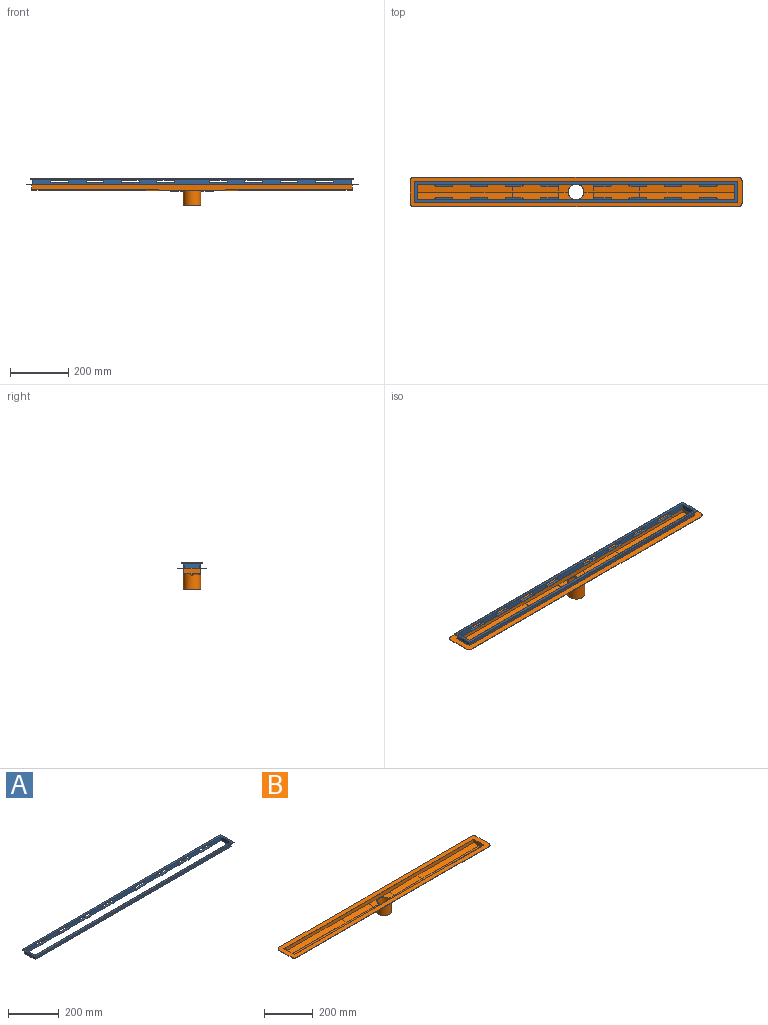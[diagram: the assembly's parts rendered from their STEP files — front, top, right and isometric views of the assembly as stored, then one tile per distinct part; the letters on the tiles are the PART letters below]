
ASSEMBLY  parts=2 mates=1
PART A: 212 faces, bbox 1112.8x73x20.6 mm
  f0: plane 1093.79x20.64mm, normal (0,1,0), area 17992.5mm2, adj f6,f7,f9,f12,f13,f17,f19,f23
  f1: plane 1096.96x19.05mm, normal (0,-1,0), area 17088.3mm2, adj f2,f6,f10,f18,f25,f32,f39,f40
  f2: plane 1109.66x69.85mm, normal (0,0,-1), area 14818.5mm2, adj f1,f5,f10,f11,f61,f63,f114,f115
  f3: plane 1112.84x3.18mm, normal (0,-1,0), area 3533.3mm2, adj f4,f7,f8,f112
  f4: plane 1112.84x73.03mm, normal (0,0,-1), area 3755mm2, adj f3,f5,f8,f11,f62,f63,f112,f115
  f5: plane 1109.66x1.59mm, normal (0,1,0), area 1761.6mm2, adj f2,f4,f11,f115
  f6: plane 1096.96x57.15mm, normal (0,0,-1), area 3654.2mm2, adj f0,f1,f9,f10,f60,f61,f113,f114
  f7: plane 1112.84x73.03mm, normal (0,0,1), area 22227.8mm2, adj f0,f3,f8,f9,f60,f62,f112,f113
  f8: plane 73.03x3.18mm, normal (1,0,0), area 231.9mm2, adj f3,f4,f7,f62
  f9: plane 53.98x20.64mm, normal (-1,0,0), area 1113.9mm2, adj f0,f6,f7,f60
  f10: plane 57.15x19.05mm, normal (1,0,0), area 1088.7mm2, adj f1,f2,f6,f61
  f11: plane 69.85x1.59mm, normal (-1,0,0), area 110.9mm2, adj f2,f4,f5,f63
  f12: plane 4.13x1.59mm, normal (-1,0,0), area 6.6mm2, adj f0,f16,f17,f18
  f13: plane 4.13x1.59mm, normal (1,0,0), area 6.6mm2, adj f0,f14,f17,f18
  f14: cylinder r=3.81mm len=3.81mm, axis (0,0,1), area 9.5mm2, adj f13,f15,f17,f18
  f15: plane 53.15x1.59mm, normal (0,1,0), area 84.4mm2, adj f14,f16,f17,f18
  f16: cylinder r=3.81mm len=3.81mm, axis (0,0,1), area 9.5mm2, adj f12,f15,f17,f18
  f17: plane 60.77x7.94mm, normal (0,0,-1), area 476.1mm2, adj f0,f12,f13,f14,f15,f16
  f18: plane 60.77x9.53mm, normal (0,0,1), area 572.6mm2, adj f1,f12,f13,f14,f15,f16,f40,f44
  f19: plane 4.13x1.59mm, normal (1,0,0), area 6.6mm2, adj f0,f20,f24,f25
  f20: cylinder r=3.81mm len=3.81mm, axis (0,0,1), area 9.5mm2, adj f19,f21,f24,f25
  f21: plane 53.15x1.59mm, normal (0,1,0), area 84.4mm2, adj f20,f22,f24,f25
  f22: cylinder r=3.81mm len=3.81mm, axis (0,0,1), area 9.5mm2, adj f21,f23,f24,f25
  f23: plane 4.13x1.59mm, normal (-1,0,0), area 6.6mm2, adj f0,f22,f24,f25
  f24: plane 60.77x7.94mm, normal (0,0,-1), area 476.1mm2, adj f0,f19,f20,f21,f22,f23
  f25: plane 60.77x9.53mm, normal (0,0,1), area 572.6mm2, adj f1,f19,f20,f21,f22,f23,f45,f49
  f26: plane 4.13x1.59mm, normal (1,0,0), area 6.6mm2, adj f0,f27,f31,f32
  f27: cylinder r=3.81mm len=3.81mm, axis (0,0,1), area 9.5mm2, adj f26,f28,f31,f32
  f28: plane 53.15x1.59mm, normal (0,1,0), area 84.4mm2, adj f27,f29,f31,f32
  f29: cylinder r=3.81mm len=3.81mm, axis (0,0,1), area 9.5mm2, adj f28,f30,f31,f32
  f30: plane 4.13x1.59mm, normal (-1,0,0), area 6.6mm2, adj f0,f29,f31,f32
  f31: plane 60.77x7.94mm, normal (0,0,-1), area 476.1mm2, adj f0,f26,f27,f28,f29,f30
  f32: plane 60.77x9.53mm, normal (0,0,1), area 572.6mm2, adj f1,f26,f27,f28,f29,f30,f50,f54
  f33: plane 4.13x1.59mm, normal (1,0,0), area 6.6mm2, adj f0,f34,f38,f39
  f34: cylinder r=3.81mm len=3.81mm, axis (0,0,1), area 9.5mm2, adj f33,f35,f38,f39
  f35: plane 53.15x1.59mm, normal (0,1,0), area 84.4mm2, adj f34,f36,f38,f39
  f36: cylinder r=3.81mm len=3.81mm, axis (0,0,1), area 9.5mm2, adj f35,f37,f38,f39
  f37: plane 4.13x1.59mm, normal (-1,0,0), area 6.6mm2, adj f0,f36,f38,f39
  f38: plane 60.77x7.94mm, normal (0,0,-1), area 476.1mm2, adj f0,f33,f34,f35,f36,f37
  f39: plane 60.77x9.53mm, normal (0,0,1), area 572.6mm2, adj f1,f33,f34,f35,f36,f37,f56,f57
  f40: plane 4.13x1.59mm, normal (1,0,0), area 6.6mm2, adj f0,f1,f18,f41
  f41: cylinder r=3.81mm len=3.81mm, axis (0,1,0), area 9.5mm2, adj f0,f1,f40,f42
  f42: plane 53.15x1.59mm, normal (0,0,-1), area 84.4mm2, adj f0,f1,f41,f43
  f43: cylinder r=3.81mm len=3.81mm, axis (0,1,0), area 9.5mm2, adj f0,f1,f42,f44
  f44: plane 4.13x1.59mm, normal (-1,0,0), area 6.6mm2, adj f0,f1,f18,f43
  f45: plane 4.13x1.59mm, normal (1,0,0), area 6.6mm2, adj f0,f1,f25,f46
  f46: cylinder r=3.81mm len=3.81mm, axis (0,1,0), area 9.5mm2, adj f0,f1,f45,f47
  f47: plane 53.15x1.59mm, normal (0,0,-1), area 84.4mm2, adj f0,f1,f46,f48
  f48: cylinder r=3.81mm len=3.81mm, axis (0,1,0), area 9.5mm2, adj f0,f1,f47,f49
  f49: plane 4.13x1.59mm, normal (-1,0,0), area 6.6mm2, adj f0,f1,f25,f48
  f50: plane 4.13x1.59mm, normal (1,0,0), area 6.6mm2, adj f0,f1,f32,f51
  f51: cylinder r=3.81mm len=3.81mm, axis (0,1,0), area 9.5mm2, adj f0,f1,f50,f52
  f52: plane 53.15x1.59mm, normal (0,0,-1), area 84.4mm2, adj f0,f1,f51,f53
  f53: cylinder r=3.81mm len=3.81mm, axis (0,1,0), area 9.5mm2, adj f0,f1,f52,f54
  f54: plane 4.13x1.59mm, normal (-1,0,0), area 6.6mm2, adj f0,f1,f32,f53
  f55: cylinder r=3.81mm len=3.81mm, axis (0,1,0), area 9.5mm2, adj f0,f1,f56,f59
  f56: plane 4.13x1.59mm, normal (-1,0,0), area 6.6mm2, adj f0,f1,f39,f55
  f57: plane 4.13x1.59mm, normal (1,0,0), area 6.6mm2, adj f0,f1,f39,f58
  f58: cylinder r=3.81mm len=3.81mm, axis (0,1,0), area 9.5mm2, adj f0,f1,f57,f59
  f59: plane 53.15x1.59mm, normal (0,0,-1), area 84.4mm2, adj f0,f1,f55,f58
  f60: plane 1093.79x20.64mm, normal (0,-1,0), area 17992.5mm2, adj f6,f7,f9,f64,f65,f69,f71,f75
  f61: plane 1096.96x19.05mm, normal (0,1,0), area 17088.3mm2, adj f2,f6,f10,f70,f77,f84,f91,f92
  f62: plane 1112.84x3.18mm, normal (0,1,0), area 3533.3mm2, adj f4,f7,f8,f112
  f63: plane 1109.66x1.59mm, normal (0,-1,0), area 1761.6mm2, adj f2,f4,f11,f115
  f64: plane 4.13x1.59mm, normal (-1,0,0), area 6.6mm2, adj f60,f68,f69,f70
  f65: plane 4.13x1.59mm, normal (1,0,0), area 6.6mm2, adj f60,f66,f69,f70
  f66: cylinder r=3.81mm len=3.81mm, axis (0,0,1), area 9.5mm2, adj f65,f67,f69,f70
  f67: plane 53.15x1.59mm, normal (0,-1,0), area 84.4mm2, adj f66,f68,f69,f70
  f68: cylinder r=3.81mm len=3.81mm, axis (0,0,1), area 9.5mm2, adj f64,f67,f69,f70
  f69: plane 60.77x7.94mm, normal (0,0,-1), area 476.1mm2, adj f60,f64,f65,f66,f67,f68
  f70: plane 60.77x9.53mm, normal (0,0,1), area 572.6mm2, adj f61,f64,f65,f66,f67,f68,f92,f96
  f71: plane 4.13x1.59mm, normal (1,0,0), area 6.6mm2, adj f60,f72,f76,f77
  f72: cylinder r=3.81mm len=3.81mm, axis (0,0,1), area 9.5mm2, adj f71,f73,f76,f77
  f73: plane 53.15x1.59mm, normal (0,-1,0), area 84.4mm2, adj f72,f74,f76,f77
  f74: cylinder r=3.81mm len=3.81mm, axis (0,0,1), area 9.5mm2, adj f73,f75,f76,f77
  f75: plane 4.13x1.59mm, normal (-1,0,0), area 6.6mm2, adj f60,f74,f76,f77
  f76: plane 60.77x7.94mm, normal (0,0,-1), area 476.1mm2, adj f60,f71,f72,f73,f74,f75
  f77: plane 60.77x9.53mm, normal (0,0,1), area 572.6mm2, adj f61,f71,f72,f73,f74,f75,f97,f101
  f78: plane 4.13x1.59mm, normal (1,0,0), area 6.6mm2, adj f60,f79,f83,f84
  f79: cylinder r=3.81mm len=3.81mm, axis (0,0,1), area 9.5mm2, adj f78,f80,f83,f84
  f80: plane 53.15x1.59mm, normal (0,-1,0), area 84.4mm2, adj f79,f81,f83,f84
  f81: cylinder r=3.81mm len=3.81mm, axis (0,0,1), area 9.5mm2, adj f80,f82,f83,f84
  f82: plane 4.13x1.59mm, normal (-1,0,0), area 6.6mm2, adj f60,f81,f83,f84
  f83: plane 60.77x7.94mm, normal (0,0,-1), area 476.1mm2, adj f60,f78,f79,f80,f81,f82
  f84: plane 60.77x9.53mm, normal (0,0,1), area 572.6mm2, adj f61,f78,f79,f80,f81,f82,f102,f106
  f85: plane 4.13x1.59mm, normal (1,0,0), area 6.6mm2, adj f60,f86,f90,f91
  f86: cylinder r=3.81mm len=3.81mm, axis (0,0,1), area 9.5mm2, adj f85,f87,f90,f91
  f87: plane 53.15x1.59mm, normal (0,-1,0), area 84.4mm2, adj f86,f88,f90,f91
  f88: cylinder r=3.81mm len=3.81mm, axis (0,0,1), area 9.5mm2, adj f87,f89,f90,f91
  f89: plane 4.13x1.59mm, normal (-1,0,0), area 6.6mm2, adj f60,f88,f90,f91
  f90: plane 60.77x7.94mm, normal (0,0,-1), area 476.1mm2, adj f60,f85,f86,f87,f88,f89
  f91: plane 60.77x9.53mm, normal (0,0,1), area 572.6mm2, adj f61,f85,f86,f87,f88,f89,f108,f109
  f92: plane 4.13x1.59mm, normal (1,0,0), area 6.6mm2, adj f60,f61,f70,f93
  f93: cylinder r=3.81mm len=3.81mm, axis (0,-1,0), area 9.5mm2, adj f60,f61,f92,f94
  f94: plane 53.15x1.59mm, normal (0,0,-1), area 84.4mm2, adj f60,f61,f93,f95
  f95: cylinder r=3.81mm len=3.81mm, axis (0,-1,0), area 9.5mm2, adj f60,f61,f94,f96
  f96: plane 4.13x1.59mm, normal (-1,0,0), area 6.6mm2, adj f60,f61,f70,f95
  f97: plane 4.13x1.59mm, normal (1,0,0), area 6.6mm2, adj f60,f61,f77,f98
  f98: cylinder r=3.81mm len=3.81mm, axis (0,-1,0), area 9.5mm2, adj f60,f61,f97,f99
  f99: plane 53.15x1.59mm, normal (0,0,-1), area 84.4mm2, adj f60,f61,f98,f100
  f100: cylinder r=3.81mm len=3.81mm, axis (0,-1,0), area 9.5mm2, adj f60,f61,f99,f101
  f101: plane 4.13x1.59mm, normal (-1,0,0), area 6.6mm2, adj f60,f61,f77,f100
  f102: plane 4.13x1.59mm, normal (1,0,0), area 6.6mm2, adj f60,f61,f84,f103
  f103: cylinder r=3.81mm len=3.81mm, axis (0,-1,0), area 9.5mm2, adj f60,f61,f102,f104
  f104: plane 53.15x1.59mm, normal (0,0,-1), area 84.4mm2, adj f60,f61,f103,f105
  f105: cylinder r=3.81mm len=3.81mm, axis (0,-1,0), area 9.5mm2, adj f60,f61,f104,f106
  f106: plane 4.13x1.59mm, normal (-1,0,0), area 6.6mm2, adj f60,f61,f84,f105
  f107: cylinder r=3.81mm len=3.81mm, axis (0,-1,0), area 9.5mm2, adj f60,f61,f108,f111
  f108: plane 4.13x1.59mm, normal (-1,0,0), area 6.6mm2, adj f60,f61,f91,f107
  f109: plane 4.13x1.59mm, normal (1,0,0), area 6.6mm2, adj f60,f61,f91,f110
  f110: cylinder r=3.81mm len=3.81mm, axis (0,-1,0), area 9.5mm2, adj f60,f61,f109,f111
  f111: plane 53.15x1.59mm, normal (0,0,-1), area 84.4mm2, adj f60,f61,f107,f110
  f112: plane 73.03x3.18mm, normal (-1,0,0), area 231.9mm2, adj f3,f4,f7,f62
  f113: plane 53.98x20.64mm, normal (1,0,0), area 1113.9mm2, adj f0,f6,f7,f60
  f114: plane 57.15x19.05mm, normal (-1,0,0), area 1088.7mm2, adj f1,f2,f6,f61
  f115: plane 69.85x1.59mm, normal (1,0,0), area 110.9mm2, adj f2,f4,f5,f63
  f116: plane 4.13x1.59mm, normal (1,0,0), area 6.6mm2, adj f0,f120,f121,f122
  f117: plane 4.13x1.59mm, normal (-1,0,0), area 6.6mm2, adj f0,f118,f121,f122
  f118: cylinder r=3.81mm len=3.81mm, axis (0,0,1), area 9.5mm2, adj f117,f119,f121,f122
  f119: plane 53.15x1.59mm, normal (0,1,0), area 84.4mm2, adj f118,f120,f121,f122
  f120: cylinder r=3.81mm len=3.81mm, axis (0,0,1), area 9.5mm2, adj f116,f119,f121,f122
  f121: plane 60.77x7.94mm, normal (0,0,-1), area 476.1mm2, adj f0,f116,f117,f118,f119,f120
  f122: plane 60.77x9.53mm, normal (0,0,1), area 572.6mm2, adj f1,f116,f117,f118,f119,f120,f144,f148
  f123: plane 4.13x1.59mm, normal (-1,0,0), area 6.6mm2, adj f0,f124,f128,f129
  f124: cylinder r=3.81mm len=3.81mm, axis (0,0,1), area 9.5mm2, adj f123,f125,f128,f129
  f125: plane 53.15x1.59mm, normal (0,1,0), area 84.4mm2, adj f124,f126,f128,f129
  f126: cylinder r=3.81mm len=3.81mm, axis (0,0,1), area 9.5mm2, adj f125,f127,f128,f129
  f127: plane 4.13x1.59mm, normal (1,0,0), area 6.6mm2, adj f0,f126,f128,f129
  f128: plane 60.77x7.94mm, normal (0,0,-1), area 476.1mm2, adj f0,f123,f124,f125,f126,f127
  f129: plane 60.77x9.53mm, normal (0,0,1), area 572.6mm2, adj f1,f123,f124,f125,f126,f127,f149,f153
  f130: plane 4.13x1.59mm, normal (-1,0,0), area 6.6mm2, adj f0,f131,f135,f136
  f131: cylinder r=3.81mm len=3.81mm, axis (0,0,1), area 9.5mm2, adj f130,f132,f135,f136
  f132: plane 53.15x1.59mm, normal (0,1,0), area 84.4mm2, adj f131,f133,f135,f136
  f133: cylinder r=3.81mm len=3.81mm, axis (0,0,1), area 9.5mm2, adj f132,f134,f135,f136
  f134: plane 4.13x1.59mm, normal (1,0,0), area 6.6mm2, adj f0,f133,f135,f136
  f135: plane 60.77x7.94mm, normal (0,0,-1), area 476.1mm2, adj f0,f130,f131,f132,f133,f134
  f136: plane 60.77x9.53mm, normal (0,0,1), area 572.6mm2, adj f1,f130,f131,f132,f133,f134,f154,f158
  f137: plane 4.13x1.59mm, normal (-1,0,0), area 6.6mm2, adj f0,f138,f142,f143
  f138: cylinder r=3.81mm len=3.81mm, axis (0,0,1), area 9.5mm2, adj f137,f139,f142,f143
  f139: plane 53.15x1.59mm, normal (0,1,0), area 84.4mm2, adj f138,f140,f142,f143
  f140: cylinder r=3.81mm len=3.81mm, axis (0,0,1), area 9.5mm2, adj f139,f141,f142,f143
  f141: plane 4.13x1.59mm, normal (1,0,0), area 6.6mm2, adj f0,f140,f142,f143
  f142: plane 60.77x7.94mm, normal (0,0,-1), area 476.1mm2, adj f0,f137,f138,f139,f140,f141
  f143: plane 60.77x9.53mm, normal (0,0,1), area 572.6mm2, adj f1,f137,f138,f139,f140,f141,f160,f161
  f144: plane 4.13x1.59mm, normal (-1,0,0), area 6.6mm2, adj f0,f1,f122,f145
  f145: cylinder r=3.81mm len=3.81mm, axis (0,1,0), area 9.5mm2, adj f0,f1,f144,f146
  f146: plane 53.15x1.59mm, normal (0,0,-1), area 84.4mm2, adj f0,f1,f145,f147
  f147: cylinder r=3.81mm len=3.81mm, axis (0,1,0), area 9.5mm2, adj f0,f1,f146,f148
  f148: plane 4.13x1.59mm, normal (1,0,0), area 6.6mm2, adj f0,f1,f122,f147
  f149: plane 4.13x1.59mm, normal (-1,0,0), area 6.6mm2, adj f0,f1,f129,f150
  f150: cylinder r=3.81mm len=3.81mm, axis (0,1,0), area 9.5mm2, adj f0,f1,f149,f151
  f151: plane 53.15x1.59mm, normal (0,0,-1), area 84.4mm2, adj f0,f1,f150,f152
  f152: cylinder r=3.81mm len=3.81mm, axis (0,1,0), area 9.5mm2, adj f0,f1,f151,f153
  f153: plane 4.13x1.59mm, normal (1,0,0), area 6.6mm2, adj f0,f1,f129,f152
  f154: plane 4.13x1.59mm, normal (-1,0,0), area 6.6mm2, adj f0,f1,f136,f155
  f155: cylinder r=3.81mm len=3.81mm, axis (0,1,0), area 9.5mm2, adj f0,f1,f154,f156
  f156: plane 53.15x1.59mm, normal (0,0,-1), area 84.4mm2, adj f0,f1,f155,f157
  f157: cylinder r=3.81mm len=3.81mm, axis (0,1,0), area 9.5mm2, adj f0,f1,f156,f158
  f158: plane 4.13x1.59mm, normal (1,0,0), area 6.6mm2, adj f0,f1,f136,f157
  f159: cylinder r=3.81mm len=3.81mm, axis (0,1,0), area 9.5mm2, adj f0,f1,f160,f163
  f160: plane 4.13x1.59mm, normal (1,0,0), area 6.6mm2, adj f0,f1,f143,f159
  f161: plane 4.13x1.59mm, normal (-1,0,0), area 6.6mm2, adj f0,f1,f143,f162
  f162: cylinder r=3.81mm len=3.81mm, axis (0,1,0), area 9.5mm2, adj f0,f1,f161,f163
  f163: plane 53.15x1.59mm, normal (0,0,-1), area 84.4mm2, adj f0,f1,f159,f162
  f164: plane 4.13x1.59mm, normal (1,0,0), area 6.6mm2, adj f60,f168,f169,f170
  f165: plane 4.13x1.59mm, normal (-1,0,0), area 6.6mm2, adj f60,f166,f169,f170
  f166: cylinder r=3.81mm len=3.81mm, axis (0,0,1), area 9.5mm2, adj f165,f167,f169,f170
  f167: plane 53.15x1.59mm, normal (0,-1,0), area 84.4mm2, adj f166,f168,f169,f170
  f168: cylinder r=3.81mm len=3.81mm, axis (0,0,1), area 9.5mm2, adj f164,f167,f169,f170
  f169: plane 60.77x7.94mm, normal (0,0,-1), area 476.1mm2, adj f60,f164,f165,f166,f167,f168
  f170: plane 60.77x9.53mm, normal (0,0,1), area 572.6mm2, adj f61,f164,f165,f166,f167,f168,f192,f196
  f171: plane 4.13x1.59mm, normal (-1,0,0), area 6.6mm2, adj f60,f172,f176,f177
  f172: cylinder r=3.81mm len=3.81mm, axis (0,0,1), area 9.5mm2, adj f171,f173,f176,f177
  f173: plane 53.15x1.59mm, normal (0,-1,0), area 84.4mm2, adj f172,f174,f176,f177
  f174: cylinder r=3.81mm len=3.81mm, axis (0,0,1), area 9.5mm2, adj f173,f175,f176,f177
  f175: plane 4.13x1.59mm, normal (1,0,0), area 6.6mm2, adj f60,f174,f176,f177
  f176: plane 60.77x7.94mm, normal (0,0,-1), area 476.1mm2, adj f60,f171,f172,f173,f174,f175
  f177: plane 60.77x9.53mm, normal (0,0,1), area 572.6mm2, adj f61,f171,f172,f173,f174,f175,f197,f201
  f178: plane 4.13x1.59mm, normal (-1,0,0), area 6.6mm2, adj f60,f179,f183,f184
  f179: cylinder r=3.81mm len=3.81mm, axis (0,0,1), area 9.5mm2, adj f178,f180,f183,f184
  f180: plane 53.15x1.59mm, normal (0,-1,0), area 84.4mm2, adj f179,f181,f183,f184
  f181: cylinder r=3.81mm len=3.81mm, axis (0,0,1), area 9.5mm2, adj f180,f182,f183,f184
  f182: plane 4.13x1.59mm, normal (1,0,0), area 6.6mm2, adj f60,f181,f183,f184
  f183: plane 60.77x7.94mm, normal (0,0,-1), area 476.1mm2, adj f60,f178,f179,f180,f181,f182
  f184: plane 60.77x9.53mm, normal (0,0,1), area 572.6mm2, adj f61,f178,f179,f180,f181,f182,f202,f206
  f185: plane 4.13x1.59mm, normal (-1,0,0), area 6.6mm2, adj f60,f186,f190,f191
  f186: cylinder r=3.81mm len=3.81mm, axis (0,0,1), area 9.5mm2, adj f185,f187,f190,f191
  f187: plane 53.15x1.59mm, normal (0,-1,0), area 84.4mm2, adj f186,f188,f190,f191
  f188: cylinder r=3.81mm len=3.81mm, axis (0,0,1), area 9.5mm2, adj f187,f189,f190,f191
  f189: plane 4.13x1.59mm, normal (1,0,0), area 6.6mm2, adj f60,f188,f190,f191
  f190: plane 60.77x7.94mm, normal (0,0,-1), area 476.1mm2, adj f60,f185,f186,f187,f188,f189
  f191: plane 60.77x9.53mm, normal (0,0,1), area 572.6mm2, adj f61,f185,f186,f187,f188,f189,f208,f209
  f192: plane 4.13x1.59mm, normal (-1,0,0), area 6.6mm2, adj f60,f61,f170,f193
  f193: cylinder r=3.81mm len=3.81mm, axis (0,-1,0), area 9.5mm2, adj f60,f61,f192,f194
  f194: plane 53.15x1.59mm, normal (0,0,-1), area 84.4mm2, adj f60,f61,f193,f195
  f195: cylinder r=3.81mm len=3.81mm, axis (0,-1,0), area 9.5mm2, adj f60,f61,f194,f196
  f196: plane 4.13x1.59mm, normal (1,0,0), area 6.6mm2, adj f60,f61,f170,f195
  f197: plane 4.13x1.59mm, normal (-1,0,0), area 6.6mm2, adj f60,f61,f177,f198
  f198: cylinder r=3.81mm len=3.81mm, axis (0,-1,0), area 9.5mm2, adj f60,f61,f197,f199
  f199: plane 53.15x1.59mm, normal (0,0,-1), area 84.4mm2, adj f60,f61,f198,f200
  f200: cylinder r=3.81mm len=3.81mm, axis (0,-1,0), area 9.5mm2, adj f60,f61,f199,f201
  f201: plane 4.13x1.59mm, normal (1,0,0), area 6.6mm2, adj f60,f61,f177,f200
  f202: plane 4.13x1.59mm, normal (-1,0,0), area 6.6mm2, adj f60,f61,f184,f203
  f203: cylinder r=3.81mm len=3.81mm, axis (0,-1,0), area 9.5mm2, adj f60,f61,f202,f204
  f204: plane 53.15x1.59mm, normal (0,0,-1), area 84.4mm2, adj f60,f61,f203,f205
  f205: cylinder r=3.81mm len=3.81mm, axis (0,-1,0), area 9.5mm2, adj f60,f61,f204,f206
  f206: plane 4.13x1.59mm, normal (1,0,0), area 6.6mm2, adj f60,f61,f184,f205
  f207: cylinder r=3.81mm len=3.81mm, axis (0,-1,0), area 9.5mm2, adj f60,f61,f208,f211
  f208: plane 4.13x1.59mm, normal (1,0,0), area 6.6mm2, adj f60,f61,f191,f207
  f209: plane 4.13x1.59mm, normal (-1,0,0), area 6.6mm2, adj f60,f61,f191,f210
  f210: cylinder r=3.81mm len=3.81mm, axis (0,-1,0), area 9.5mm2, adj f60,f61,f209,f211
  f211: plane 53.15x1.59mm, normal (0,0,-1), area 84.4mm2, adj f60,f61,f207,f210
PART B: 46 faces, bbox 1144.6x101.6x73.1 mm
  f0: plane 1144.59x101.6mm, normal (0,0,1), area 53277.2mm2, adj f2,f9,f12,f17,f18,f19,f21,f26
  f1: plane 119.06x28.58mm, normal (0,-0.09,1), area 2259.1mm2, adj f2,f11,f23,f36,f44,f45
  f2: plane 1100.14x19.73mm, normal (0,-1,0), area 19076.9mm2, adj f0,f1,f17,f23,f25,f32,f36,f38
  f3: plane 59.53x30.16mm, normal (0,-0.09,-1), area 1085.2mm2, adj f6,f7,f28,f41
  f4: plane 59.53x30.16mm, normal (0,-0.09,-1), area 1085.2mm2, adj f5,f7,f13,f41
  f5: plane 59.53x30.16mm, normal (0,0.09,-1), area 1085.2mm2, adj f4,f20,f22,f41
  f6: plane 59.53x30.16mm, normal (0,0.09,-1), area 1085.2mm2, adj f3,f20,f35,f41
  f7: plane 1103.31x19.59mm, normal (0,-1,0), area 19000.4mm2, adj f3,f4,f8,f10,f13,f15,f27,f28
  f8: plane 60.33x19.06mm, normal (1,0,0), area 1070mm2, adj f7,f10,f15,f20,f24
  f9: plane 1119.19x1.59mm, normal (0,-1,0), area 1776.7mm2, adj f0,f10,f19,f34
  f10: plane 1144.59x101.6mm, normal (0,0,-1), area 49594.3mm2, adj f7,f8,f9,f18,f19,f20,f21,f26
  f11: plane 119.06x28.58mm, normal (0,0.09,1), area 2274.3mm2, adj f1,f12,f14,f29,f45
  f12: plane 1100.14x19.73mm, normal (0,1,0), area 19094.4mm2, adj f0,f11,f14,f16,f17,f29,f31,f32
  f13: plane 160.34x30.16mm, normal (0.02,-0.09,-1), area 4855.6mm2, adj f4,f7,f15,f22
  f14: plane 160.34x28.58mm, normal (-0.02,0.09,1), area 4600mm2, adj f11,f12,f16,f23
  f15: plane 331.79x30.16mm, normal (0,-0.09,-1), area 10045.8mm2, adj f7,f8,f13,f24
  f16: plane 330.2x28.58mm, normal (0,0.09,1), area 9471.5mm2, adj f12,f14,f17,f25
  f17: plane 57.15x19.05mm, normal (-1,0,0), area 1017.3mm2, adj f0,f2,f12,f16,f25
  f18: plane 76.2x1.59mm, normal (1,0,0), area 121mm2, adj f0,f10,f19,f26
  f19: cylinder r=12.7mm len=12.7mm, axis (0,0,1), area 31.7mm2, adj f0,f9,f10,f18
  f20: plane 1103.31x19.59mm, normal (0,1,0), area 19000.4mm2, adj f5,f6,f8,f10,f22,f24,f27,f35
  f21: plane 1119.19x1.59mm, normal (0,1,0), area 1776.7mm2, adj f0,f10,f26,f39
  f22: plane 160.34x30.16mm, normal (0.02,0.09,-1), area 4855.6mm2, adj f5,f13,f20,f24
  f23: plane 160.34x28.58mm, normal (-0.02,-0.09,1), area 4600mm2, adj f1,f2,f14,f25
  f24: plane 331.79x30.16mm, normal (0,0.09,-1), area 10045.8mm2, adj f8,f15,f20,f22
  f25: plane 330.2x28.58mm, normal (0,-0.09,1), area 9471.5mm2, adj f2,f16,f17,f23
  f26: cylinder r=12.7mm len=12.7mm, axis (0,0,1), area 31.7mm2, adj f0,f10,f18,f21
  f27: plane 60.33x19.06mm, normal (-1,0,0), area 1070mm2, adj f7,f10,f20,f30,f37
  f28: plane 160.34x30.16mm, normal (-0.02,-0.09,-1), area 4855.6mm2, adj f3,f7,f30,f35
  f29: plane 160.34x28.58mm, normal (0.02,0.09,1), area 4600mm2, adj f11,f12,f31,f36
  f30: plane 331.79x30.16mm, normal (0,-0.09,-1), area 10045.8mm2, adj f7,f27,f28,f37
  f31: plane 330.2x28.58mm, normal (0,0.09,1), area 9471.5mm2, adj f12,f29,f32,f38
  f32: plane 57.15x19.05mm, normal (1,0,0), area 1017.3mm2, adj f0,f2,f12,f31,f38
  f33: plane 76.2x1.59mm, normal (-1,0,0), area 121mm2, adj f0,f10,f34,f39
  f34: cylinder r=12.7mm len=12.7mm, axis (0,0,1), area 31.7mm2, adj f0,f9,f10,f33
  f35: plane 160.34x30.16mm, normal (-0.02,0.09,-1), area 4855.6mm2, adj f6,f20,f28,f37
  f36: plane 160.34x28.58mm, normal (0.02,-0.09,1), area 4600mm2, adj f1,f2,f29,f38
  f37: plane 331.79x30.16mm, normal (0,0.09,-1), area 10045.8mm2, adj f20,f27,f30,f35
  f38: plane 330.2x28.58mm, normal (0,-0.09,1), area 9471.5mm2, adj f2,f31,f32,f36
  f39: cylinder r=12.7mm len=12.7mm, axis (0,0,1), area 31.7mm2, adj f0,f10,f21,f33
  f40: plane 60.33x60.33mm, normal (0,0,-1), area 570mm2, adj f41,f42
  f41: cylinder r=30.16mm len=60.33mm, axis (0,0,-1), area 9643.8mm2, adj f3,f4,f5,f6,f40
  f42: cylinder r=26.99mm len=53.98mm, axis (0,0,-1), area 8598.7mm2, adj f40,f44,f45
  f43: extruded ~7.92x3.36mm, area 17.6mm2, adj f0,f2
  f44: extruded ~53.98x27.13mm, area 135.9mm2, adj f1,f42,f45
  f45: extruded ~53.98x27.13mm, area 134.9mm2, adj f1,f11,f42,f44
PLACE A t=(-137.84,-45.82,105.84)mm
PLACE B t=(-137.84,-45.82,86.79)mm fixed
MATE fastened A.f6 <-> B.f42  axis (0,0,-1) through (-137.84,-45.82,85.2)mm
